# Revit family: PRD_FrankeWS_Prss-actnSlf-clsngPllrTps_F3SSelf-closingPillarTap_F3SV1004
name_source: partatom
category: Plumbing Fixtures
revit_build: Autodesk Revit 2018 (Build: 20190510_1515(x64)
units: mm (PartAtom-declared; Revit-internal decimal feet)

## family parameters
Always vertical = Yes
Cut with Voids When Loaded = No
OmniClass Number = 23.45.55.14
OmniClass Title = Single Faucets
Part Type = Normal
Room Calculation Point = No
Round Connector Dimension = Use Diameter
Shared = No
Work Plane-Based = Yes

## types (1)
- F3SV1004
    AdjustableFlowTime = Yes
    AssetType = Fixed
    BIMObjectName = PRD_AR_Press-actionSelf-closingPillarTaps_F3SSelf-closingPillarTap_F3SV1004
    Category = Pr_40_20_87_66, Press-action self-closing pillar taps
    Color = Chrome
    Default Elevation = 0 mm  [stored 0 ft]
    Depressurised = No
    Description = F3S self-closing DN 15 pillar tap for sanitary facilities. Self-closing cartridge, hydraulically controlled, self-closing, stepless adjustment of flow duration. With anti-blocking system 2 (ABS2) for safety switch-off when permanently active. For connection to pre-mixed hot water or cold water. High-polished, chrome-plated brass housing. Aerator with an integrated flow rate controller 3.0 l/min.
    DiameterNominal = 15 mm
    DurationUnit = year
    FaucetFunction = Mixed
    FaucetOperation = TimedSelfClosing
    FaucetType = Pillar
    Features = For connection to pre-mixed hot water or cold water. High-polished, chrome-plated brass housing.
    Finish = Polished chrome
    Flow = 0.1 L/s
    FunctionalPrinciple = Hydraulic self-closing
    GrossWeight = 1.14 kg
    HygieneFlushing = No
    IfcExportAs = IfcValveType
    IfcExportType = FAUCET
    InletSize = DN 15
    MainMaterial = PRD_AR_ChromatedBrass_HighPolished
    Manufacturer = KWC Group AG
    ManufacturerName = KWC Group AG
    ManufacturerURL = www.kwc.com
    Material = Brass
    Model = F3SV1004
    ModelNumber = 2030049135
    ModelReference = F3SV1004
    NBSDescription = Taps and water supply fittings for washbasins and troughs
    NBSReference = 45-35-70/371
    Name = F3S Self-closing pillar tap F3SV1004
    NetWeight = 1 kg
    NominalDepth = 0 mm  [stored 0 ft]
    NominalHeight = 0 mm  [stored 0 ft]
    NominalWidth = 0 mm  [stored 0 ft]
    ProductCode = 208.0599.911
    ProductInformation = https://pim.kwc.com
    ProtectiveShutdown = Yes
    Shape = Pillar
    ThermalDisinfection = No
    TypeOfMixing = No mixing
    TypeOfMounting = Tap hole
    TypeOfOperation = Manual operation
    TypeOfTap = Pillar tap
    URL = www.kwc.com
    Uniclass2015Code = Pr_40_20_87_66
    Uniclass2015Title = Press-action self-closing pillar taps
    Uniclass2015Version = Products v1.17
    Version = 1
    WarrantyDurationUnit = year

note: [stored X ft] marks values corroborated as IEEE doubles in the binary element streams (Revit-internal decimal feet)

## geometry (parser evidence)
native form markers: Sweep x6
no freeform markers — native parametric forms only
